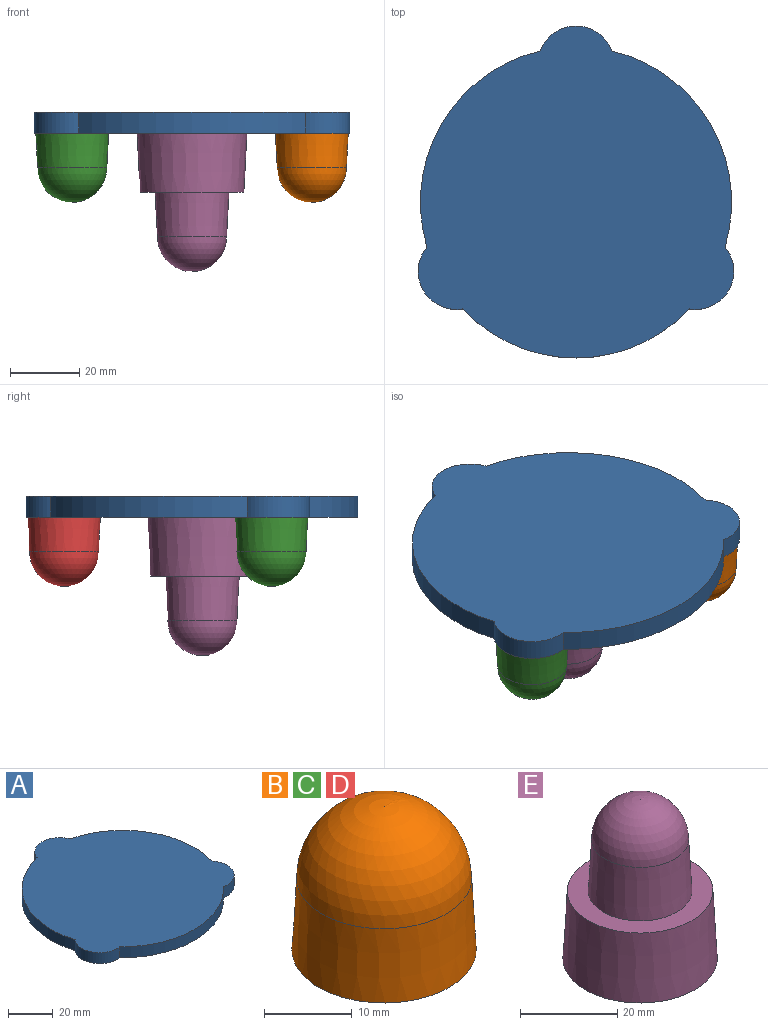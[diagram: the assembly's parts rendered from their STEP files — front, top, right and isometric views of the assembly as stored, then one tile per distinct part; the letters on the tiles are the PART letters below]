
ASSEMBLY  parts=5 mates=4
PART A: 8 faces, bbox 91.3x96x6 mm
  f0: cylinder r=45mm len=56.76mm, axis (0,0,-1), area 440.5mm2, adj f1,f5,f6,f7
  f1: cylinder r=11mm len=20.65mm, axis (0,0,-1), area 160.8mm2, adj f0,f2,f6,f7
  f2: cylinder r=45mm len=56.76mm, axis (0,0,-1), area 440.5mm2, adj f1,f3,f6,f7
  f3: cylinder r=11mm len=18.04mm, axis (0,0,-1), area 160.8mm2, adj f2,f4,f6,f7
  f4: cylinder r=45mm len=65.54mm, axis (0,0,-1), area 440.5mm2, adj f3,f5,f6,f7
  f5: cylinder r=11mm len=18.04mm, axis (0,0,-1), area 160.8mm2, adj f0,f4,f6,f7
  f6: plane 96x91.28mm, normal (0,0,1), area 6636.5mm2, adj f0,f1,f2,f3,f4,f5
  f7: plane 96x91.28mm, normal (0,0,-1), area 6636.5mm2, adj f0,f1,f2,f3,f4,f5
PART B: 3 faces, bbox 21x21x20 mm
  f0: cone r=10mm half-angle=3deg, axis (0,0,-1), area 645.7mm2, adj f1,f2
  f1: plane 21.05x21.05mm, normal (0,0,-1), area 348mm2, adj f0
  f2: sphere r=10mm, area 628.3mm2, adj f0
PART C: same geometry as B
PART D: same geometry as B
PART E: 5 faces, bbox 31.8x31.8x40 mm
  f0: cone r=10mm half-angle=3deg, axis (0,0,-1), area 845.8mm2, adj f1,f3
  f1: sphere r=10mm, area 628.3mm2, adj f0
  f2: cone r=15mm half-angle=3deg, axis (0,0,-1), area 1652.1mm2, adj f3,f4
  f3: plane 30x30mm, normal (0,0,1), area 348.4mm2, adj f0,f2
  f4: plane 31.78x31.78mm, normal (0,0,-1), area 793.3mm2, adj f2
PLACE A t=(0,0,-6)mm
PLACE B rot(axis=(1,0,0),180deg) t=(34.64,-20,-6)mm
PLACE C rot(axis=(1,0,0),180deg) t=(-34.64,-20,-6)mm
PLACE D rot(axis=(1,0,0),180deg) t=(0,40,-6)mm
PLACE E rot(axis=(1,0,0),180deg) t=(0,0,-6)mm
MATE fastened D.f0 <-> A.f1  axis (0,0,1) through (0,40,-6)mm
MATE fastened C.f0 <-> A.f3  axis (0,0,1) through (-34.64,-20,-6)mm
MATE fastened B.f0 <-> A.f5  axis (0,0,1) through (34.64,-20,-6)mm
MATE fastened E.f0 <-> A.f4  axis (0,0,1) through (0,0,-6)mm
